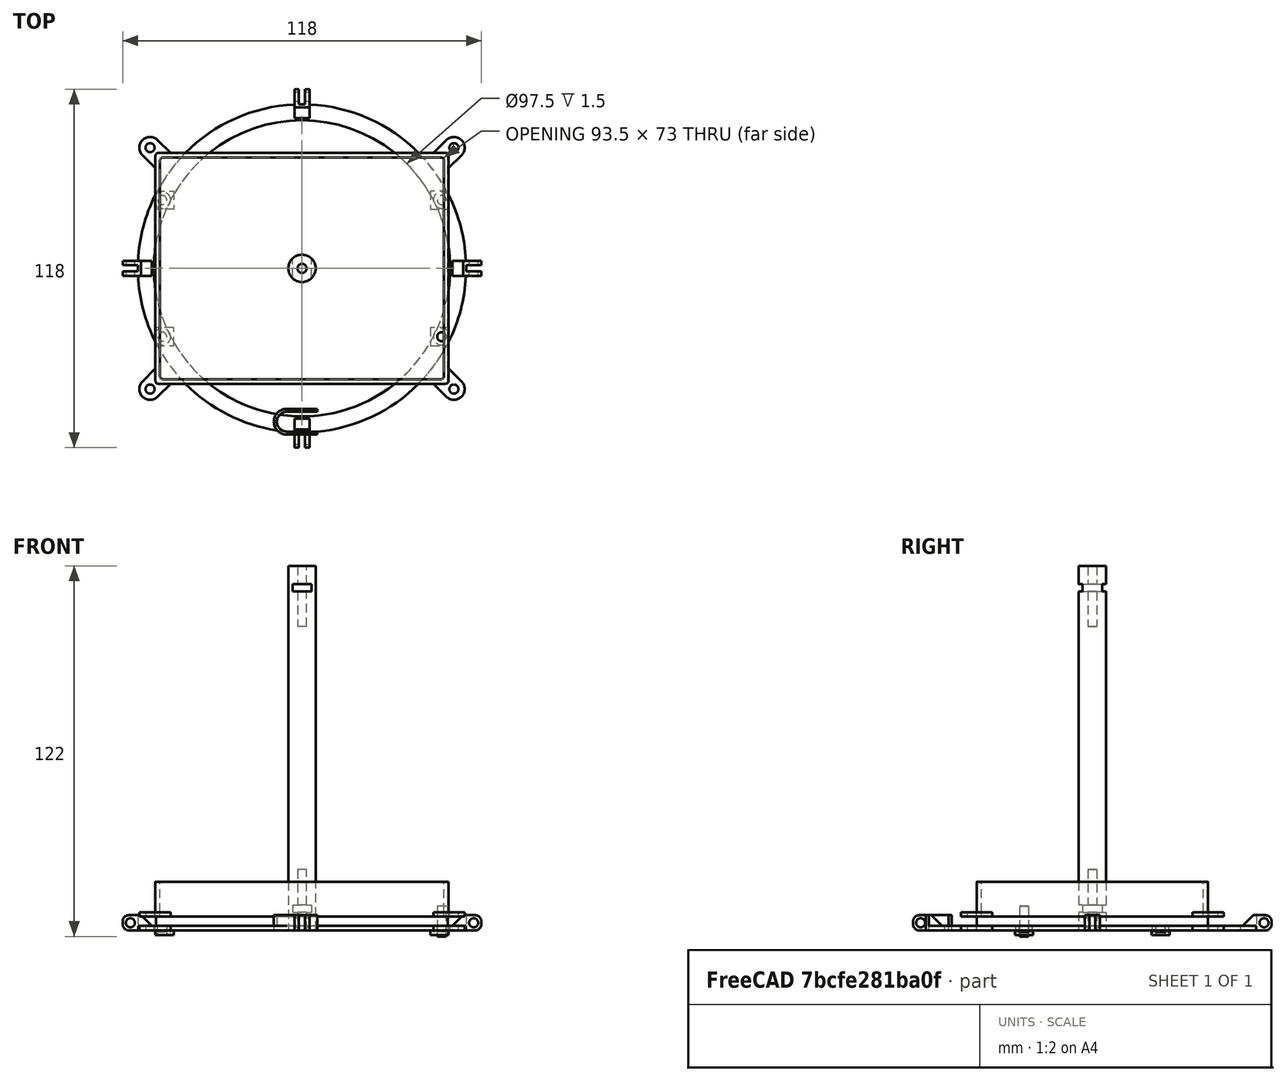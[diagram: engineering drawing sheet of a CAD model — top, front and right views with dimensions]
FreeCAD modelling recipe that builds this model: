
FCSTD DOCUMENT  (FreeCAD 0.20R29177 (Git))
Label: LSC-holder04-Robot
License: All rights reserved
LicenseURL: http://en.wikipedia.org/wiki/All_rights_reserved
objects: Part::Cut×12, Part::Box×11, Sketcher::SketchObject×9, Part::Cylinder×8, PartDesign::Pad×6, PartDesign::Body×4, Part::Fillet×4, Part::Chamfer×4, Part::Fuse×4, PartDesign::Pocket×3, Mesh::Feature×2, Spreadsheet::Sheet×1, PartDesign::Fillet×1
note: 76 computed .brp shape members not serialized (recipe doc carries the construction recipe); baked Part::Feature solids carry a one-line shape summary decoded from their .brp

FEATURE [Mesh::Feature] surface  label="ReferenceBase"
  Placement = pos=(50,-25.5,5.75) rot=(1,0,0;1.5708rad)
  expr: .Placement.Base.x = 0
FEATURE [Sketcher::SketchObject] Sketch  label="HolderBaseMain001"
  FullyConstrained = true
  MapMode = 5
  Support = -> [XY_Plane]
  expr: Constraints[2] = <<params>>.lcLength
  expr: Constraints[3] = <<params>>.lcWidth
  expr: Constraints[8] = <<params>>.lcWidth - 10
  expr: Constraints[9] = <<params>>.lcLength - 10
  sketch-geometry (24):
    g0: GeomPoint X=-48.25 Y=-38 Z=0
    g1: LineSegment StartX=-48.25 StartY=-33 StartZ=0 EndX=-48.25 EndY=33 EndZ=0
    g2: GeomPoint X=-48.25 Y=38 Z=0
    g3: LineSegment StartX=-43.25 StartY=38 StartZ=0 EndX=43.25 EndY=38 EndZ=0
    g4: GeomPoint X=48.25 Y=38 Z=0
    g5: LineSegment StartX=43.25 StartY=-38 StartZ=0 EndX=-43.25 EndY=-38 EndZ=0
    g6: LineSegment StartX=48.25 StartY=33 StartZ=0 EndX=48.25 EndY=-33 EndZ=0
    g7: GeomPoint X=48.25 Y=-38 Z=0
    g8: LineSegment StartX=43.25 StartY=-38 StartZ=0 EndX=47.4926 EndY=-42.2426 EndZ=0
    g9: LineSegment StartX=48.25 StartY=-33 StartZ=0 EndX=52.4926 EndY=-37.2426 EndZ=0
    g10: ArcOfCircle CenterX=49.9926 CenterY=-39.7426 CenterZ=0 NormalX=0 NormalY=0 NormalZ=1 AngleXU=0 Radius=3.53553 StartAngle=3.92699 EndAngle=7.06858
    g11: Circle CenterX=49.9926 CenterY=-39.7426 CenterZ=0 NormalX=0 NormalY=0 NormalZ=1 AngleXU=0 Radius=1.5
    g12: LineSegment StartX=43.25 StartY=38 StartZ=0 EndX=47.4926 EndY=42.2426 EndZ=0
    g13: LineSegment StartX=48.25 StartY=33 StartZ=0 EndX=52.4926 EndY=37.2426 EndZ=0
    g14: LineSegment StartX=-48.25 StartY=33 StartZ=0 EndX=-52.4926 EndY=37.2426 EndZ=0
    g15: LineSegment StartX=-43.25 StartY=38 StartZ=0 EndX=-47.4926 EndY=42.2426 EndZ=0
    g16: LineSegment StartX=-48.25 StartY=-33 StartZ=0 EndX=-52.4926 EndY=-37.2426 EndZ=0
    g17: LineSegment StartX=-43.25 StartY=-38 StartZ=0 EndX=-47.4926 EndY=-42.2426 EndZ=0
    g18: ArcOfCircle CenterX=49.9926 CenterY=39.7426 CenterZ=0 NormalX=0 NormalY=0 NormalZ=1 AngleXU=0 Radius=3.53553 StartAngle=5.49779 EndAngle=8.63938
    g19: ArcOfCircle CenterX=-49.9926 CenterY=39.7426 CenterZ=0 NormalX=0 NormalY=0 NormalZ=1 AngleXU=0 Radius=3.53553 StartAngle=0.785398 EndAngle=3.92699
    g20: ArcOfCircle CenterX=-49.9926 CenterY=-39.7426 CenterZ=0 NormalX=0 NormalY=0 NormalZ=1 AngleXU=0 Radius=3.53553 StartAngle=2.35619 EndAngle=5.49779
    g21: Circle CenterX=-49.9926 CenterY=-39.7426 CenterZ=0 NormalX=0 NormalY=0 NormalZ=1 AngleXU=0 Radius=1.5
    g22: Circle CenterX=-49.9926 CenterY=39.7426 CenterZ=0 NormalX=0 NormalY=0 NormalZ=1 AngleXU=0 Radius=1.5
    g23: Circle CenterX=49.9926 CenterY=39.7426 CenterZ=0 NormalX=0 NormalY=0 NormalZ=1 AngleXU=0 Radius=1.5
  constraints (64):
    c: Vertical(g1)
    c: Horizontal(g3)
    c: DistanceX(g2,g4) = 96.5
    c: DistanceY(g0,g2) = 76
    c: Horizontal(g5)
    c: Vertical(g6)
    c: Equal(g5,g3)
    c: Equal(g1,g6)
    c: DistanceY(g6,g6) = 66
    c: DistanceX(g3,g3) = 86.5
    c: DistanceX(g0) = -48.25
    c: DistanceY(g0) = -38
    c: DistanceX(g5) = -43.25
    c: DistanceY(g5) = -38
    c: DistanceX(g1) = -48.25
    c: DistanceY(g1) = -33
    c: Symmetric(g2,g7,g-1)
    c: Symmetric(g4,g0,g-1)
    c: Symmetric(g3,g5,g-1)
    c: Symmetric(g1,g6,g-1)
    c: Coincident(g8,g5)
    c: Coincident(g9,g6)
    c: Angle(g8) = -0.785398
    c: Angle(g9) = -0.785398
    c: Coincident(g10,g9)
    c: Coincident(g10,g8)
    c: Coincident(g11,g10)
    c: Distance(g8) = 6
    c: Diameter(g11) = 3
    c: Angle(g10) = 3.14159
    c: Coincident(g12,g3)
    c: Coincident(g13,g6)
    c: Coincident(g14,g1)
    c: Coincident(g15,g3)
    c: Angle(g13) = 0.785398
    c: Angle(g12) = 0.785398
    c: Angle(g15) = 2.35619
    c: Angle(g14) = 2.35619
    c: Coincident(g16,g1)
    c: Coincident(g17,g5)
    c: Angle(g16) = -2.35619
    c: Angle(g17) = -2.35619
    c: Equal(g16,g17)
    c: Equal(g17,g8)
    c: Equal(g8,g9)
    c: Equal(g9,g13)
    c: Equal(g13,g12)
    c: Equal(g12,g14)
    c: Equal(g14,g15)
    c: Coincident(g18,g12)
    c: Coincident(g18,g13)
    c: Angle(g18) = 3.14159
    c: Coincident(g19,g15)
    c: Coincident(g19,g14)
    c: Angle(g19) = 3.14159
    c: Coincident(g20,g16)
    c: Coincident(g20,g17)
    c: Angle(g20) = 3.14159
    c: Coincident(g21,g20)
    c: Diameter(g21) = 3
    c: Coincident(g22,g19)
    c: Diameter(g22) = 3
    c: Coincident(g23,g18)
    c: Diameter(g23) = 3
FEATURE [Spreadsheet::Sheet] Spreadsheet  label="params"
  cells = A2(lcLength)=96.5; A3(lcWidth)=76; A4(lcHeight)=2; A5(screwsHDist)=92; A6(screwsVDist)=45; A7(columnHeight)=120
FEATURE [PartDesign::Pad] Pad  label="HolderBaseMain"
  Direction = (0,0,1)
  Length = 1.5
  Length2 = 10
  Profile = -> Sketch
  ReferenceAxis = -> Sketch [N_Axis]
  Type = 0
FEATURE [Sketcher::SketchObject] Sketch001  label="ScrewsExtra001"
  FullyConstrained = true
  MapMode = 5
  Placement = pos=(0,0,0) rot=(1,0,0;3.14159rad)
  Support = -> [Pad]
  expr: Constraints[14] = (<<params>>.lcLength - <<params>>.screwsHDist) / 2
  expr: Constraints[25] = (<<params>>.lcLength - <<params>>.screwsHDist) / 2
  expr: Constraints[2] = <<params>>.screwsVDist
  expr: Constraints[3] = <<params>>.screwsHDist
  expr: Constraints[42] = (<<params>>.lcLength - <<params>>.screwsHDist) / 2
  expr: Constraints[43] = (<<params>>.lcLength - <<params>>.screwsHDist) / 2
  sketch-geometry (20):
    g0: GeomPoint X=-46 Y=22.5 Z=0
    g1: GeomPoint X=-46 Y=-22.5 Z=0
    g2: GeomPoint X=46 Y=-22.5 Z=0
    g3: GeomPoint X=46 Y=22.5 Z=0
    g4: LineSegment StartX=-48.25 StartY=25.5 StartZ=0 EndX=-42.25 EndY=25.5 EndZ=0
    g5: LineSegment StartX=-42.25 StartY=25.5 StartZ=0 EndX=-42.25 EndY=19.5 EndZ=0
    g6: LineSegment StartX=-42.25 StartY=19.5 StartZ=0 EndX=-48.25 EndY=19.5 EndZ=0
    g7: LineSegment StartX=-48.25 StartY=19.5 StartZ=0 EndX=-48.25 EndY=25.5 EndZ=0
    g8: LineSegment StartX=-42.25 StartY=-19.5 StartZ=0 EndX=-48.25 EndY=-19.5 EndZ=0
    g9: LineSegment StartX=-48.25 StartY=-19.5 StartZ=0 EndX=-48.25 EndY=-25.5 EndZ=0
    g10: LineSegment StartX=-48.25 StartY=-25.5 StartZ=0 EndX=-42.25 EndY=-25.5 EndZ=0
    g11: LineSegment StartX=-42.25 StartY=-25.5 StartZ=0 EndX=-42.25 EndY=-19.5 EndZ=0
    g12: LineSegment StartX=42.25 StartY=25.5 StartZ=0 EndX=48.25 EndY=25.5 EndZ=0
    g13: LineSegment StartX=48.25 StartY=25.5 StartZ=0 EndX=48.25 EndY=19.5 EndZ=0
    g14: LineSegment StartX=48.25 StartY=19.5 StartZ=0 EndX=42.25 EndY=19.5 EndZ=0
    g15: LineSegment StartX=42.25 StartY=19.5 StartZ=0 EndX=42.25 EndY=25.5 EndZ=0
    g16: LineSegment StartX=42.25 StartY=-19.5 StartZ=0 EndX=48.25 EndY=-19.5 EndZ=0
    g17: LineSegment StartX=48.25 StartY=-19.5 StartZ=0 EndX=48.25 EndY=-25.5 EndZ=0
    g18: LineSegment StartX=48.25 StartY=-25.5 StartZ=0 EndX=42.25 EndY=-25.5 EndZ=0
    g19: LineSegment StartX=42.25 StartY=-25.5 StartZ=0 EndX=42.25 EndY=-19.5 EndZ=0
  constraints (54):
    c: Symmetric(g0,g2,g-1)
    c: Symmetric(g3,g1,g-1)
    c: DistanceY(g2,g3) = 45
    c: DistanceX(g0,g3) = 92
    c: DistanceX(g2,g3) = 0
    c: DistanceY(g1,g2) = 0
    c: Coincident(g4,g5)
    c: Coincident(g5,g6)
    c: Coincident(g6,g7)
    c: Coincident(g7,g4)
    c: Horizontal(g4)
    c: Horizontal(g6)
    c: Vertical(g5)
    c: Vertical(g7)
    c: DistanceX(g4,g0) = 2.25
    c: DistanceY(g5,g5) = 6
    c: DistanceY(g0,g4) = 3
    c: Coincident(g8,g9)
    c: Coincident(g9,g10)
    c: Coincident(g10,g11)
    c: Coincident(g11,g8)
    c: Horizontal(g8)
    c: Horizontal(g10)
    c: Vertical(g9)
    c: Vertical(g11)
    c: DistanceX(g8,g1) = 2.25
    c: Coincident(g12,g13)
    c: Coincident(g13,g14)
    c: Coincident(g14,g15)
    c: Coincident(g15,g12)
    c: Horizontal(g12)
    c: Horizontal(g14)
    c: Vertical(g13)
    c: Vertical(g15)
    c: Coincident(g16,g17)
    c: Coincident(g17,g18)
    c: Coincident(g18,g19)
    c: Coincident(g19,g16)
    c: Horizontal(g16)
    c: Horizontal(g18)
    c: Vertical(g17)
    c: Vertical(g19)
    c: DistanceX(g3,g12) = 2.25
    c: DistanceX(g2,g16) = 2.25
    c: Equal(g4,g5)
    c: Equal(g5,g8)
    c: Equal(g8,g11)
    c: Equal(g11,g19)
    c: Equal(g19,g16)
    c: Equal(g16,g15)
    c: Equal(g15,g12)
    c: DistanceY(g1,g8) = 3
    c: DistanceY(g2,g16) = 3
    c: DistanceY(g3,g12) = 3
FEATURE [PartDesign::Pad] Pad001  label="ScrewsExtra"
  BaseFeature = -> Pad
  Direction = (0,0,-1)
  Length = 1.5
  Length2 = 10
  Profile = -> Sketch001
  ReferenceAxis = -> Sketch001 [N_Axis]
  Type = 0
FEATURE [Part::Cylinder] Cylinder  label="RefScrew"
  Angle = 360
  AttacherType = Attacher::AttachEngine3D
  FirstAngle = 0
  Height = 10
  Placement = pos=(46,-22.5,-2) rot=(0,0,1;0rad)
  Radius = 1.5
  SecondAngle = 0
FEATURE [Sketcher::SketchObject] Sketch002  label="ScrewsFull001"
  FullyConstrained = true
  MapMode = 5
  Placement = pos=(0,0,1.5) rot=(0,0,1;0rad)
  Support = -> [Pad001]
  expr: Constraints[2] = <<params>>.screwsHDist
  expr: Constraints[3] = <<params>>.screwsVDist
  sketch-geometry (4):
    g0: Circle CenterX=-46 CenterY=22.5 CenterZ=0 NormalX=0 NormalY=0 NormalZ=1 AngleXU=0 Radius=1.5
    g1: Circle CenterX=-46 CenterY=-22.5 CenterZ=0 NormalX=0 NormalY=0 NormalZ=1 AngleXU=0 Radius=1.5
    g2: Circle CenterX=46 CenterY=22.5 CenterZ=0 NormalX=0 NormalY=0 NormalZ=1 AngleXU=0 Radius=1.5
    g3: Circle CenterX=46 CenterY=-22.5 CenterZ=0 NormalX=0 NormalY=0 NormalZ=1 AngleXU=0 Radius=1.5
  constraints (10):
    c: Symmetric(g0,g3,g-1)
    c: Symmetric(g2,g1,g-1)
    c: DistanceX(g0,g2) = 92
    c: DistanceY(g3,g2) = 45
    c: DistanceX(g3,g2) = 0
    c: DistanceY(g1,g3) = 0
    c: Equal(g0,g1)
    c: Equal(g0,g3)
    c: Equal(g0,g2)
    c: Diameter(g0) = 3
FEATURE [PartDesign::Pocket] Pocket  label="ScrewsFull"
  BaseFeature = -> Pad001
  Direction = (0,0,-1)
  Length = 5
  Length2 = 5
  Profile = -> Sketch002
  ReferenceAxis = -> Sketch002 [N_Axis]
  Type = 1
FEATURE [Sketcher::SketchObject] Sketch003  label="ScrewsHead001"
  FullyConstrained = true
  MapMode = 5
  Placement = pos=(0,0,1.5) rot=(0,0,1;0rad)
  Support = -> [Pocket]
  expr: Constraints[2] = <<params>>.screwsVDist
  expr: Constraints[3] = <<params>>.screwsHDist
  sketch-geometry (4):
    g0: Circle CenterX=46 CenterY=22.5 CenterZ=0 NormalX=0 NormalY=0 NormalZ=1 AngleXU=0 Radius=2.75
    g1: Circle CenterX=-46 CenterY=22.5 CenterZ=0 NormalX=0 NormalY=0 NormalZ=1 AngleXU=0 Radius=2.75
    g2: Circle CenterX=-46 CenterY=-22.5 CenterZ=0 NormalX=0 NormalY=0 NormalZ=1 AngleXU=0 Radius=2.75
    g3: Circle CenterX=46 CenterY=-22.5 CenterZ=0 NormalX=0 NormalY=0 NormalZ=1 AngleXU=0 Radius=2.75
  constraints (10):
    c: Symmetric(g1,g3,g-1)
    c: Symmetric(g0,g2,g-1)
    c: DistanceY(g3,g0) = 45
    c: DistanceX(g1,g0) = 92
    c: DistanceX(g0,g3) = 0
    c: DistanceY(g3,g2) = 0
    c: Equal(g1,g0)
    c: Equal(g1,g2)
    c: Equal(g1,g3)
    c: Diameter(g1) = 5.5
FEATURE [PartDesign::Pocket] Pocket001  label="ScrewsHead"
  BaseFeature = -> Pocket
  Direction = (0,0,-1)
  Length = 2
  Length2 = 5
  Profile = -> Sketch003
  ReferenceAxis = -> Sketch003 [N_Axis]
  Type = 0
FEATURE [PartDesign::Body] Body  label="HolderBase"
  Group = -> [Sketch,Pad,Sketch001,Pad001,Sketch002,Pocket,Sketch003,Pocket001]
  Origin = -> Origin
  Tip = -> Pocket001
FEATURE [Sketcher::SketchObject] Sketch004  label="HolderMain001"
  FullyConstrained = true
  MapMode = 5
  Support = -> [XY_Plane001]
  sketch-geometry (8):
    g0: LineSegment StartX=-5 StartY=4.25 StartZ=0 EndX=5 EndY=4.25 EndZ=0
    g1: LineSegment StartX=5 StartY=4.25 StartZ=0 EndX=5 EndY=3.25 EndZ=0
    g2: LineSegment StartX=5 StartY=3.25 StartZ=0 EndX=-4.99602 EndY=3.25 EndZ=0
    g3: LineSegment StartX=4.99602 StartY=-3.25 StartZ=0 EndX=-5.00398 EndY=-3.25 EndZ=0
    g4: LineSegment StartX=-5.00002 StartY=-4.25 StartZ=0 EndX=4.99602 EndY=-4.25 EndZ=0
    g5: LineSegment StartX=4.99602 StartY=-4.25 StartZ=0 EndX=4.99602 EndY=-3.25 EndZ=0
    g6: ArcOfCircle CenterX=-5 CenterY=0 CenterZ=0 NormalX=0 NormalY=0 NormalZ=1 AngleXU=0 Radius=3.25 StartAngle=1.56957 EndAngle=4.71117
    g7: ArcOfCircle CenterX=-5 CenterY=0 CenterZ=0 NormalX=0 NormalY=0 NormalZ=1 AngleXU=0 Radius=4.25 StartAngle=1.5708 EndAngle=4.71238
  constraints (24):
    c: Coincident(g0,g1)
    c: Coincident(g1,g2)
    c: Horizontal(g0)
    c: Horizontal(g2)
    c: Vertical(g1)
    c: Coincident(g4,g5)
    c: Coincident(g5,g3)
    c: Horizontal(g3)
    c: Horizontal(g4)
    c: Vertical(g5)
    c: Symmetric(g2,g3,g-1)
    c: DistanceY(g3,g2) = 6.5
    c: Equal(g1,g5)
    c: DistanceY(g1,g1) = 1
    c: Equal(g0,g3)
    c: DistanceX(g0,g0) = 10
    c: DistanceX(g-1,g1) = 5
    c: PointOnObject(g6,g-1)
    c: Coincident(g6,g2)
    c: Coincident(g6,g3)
    c: Coincident(g7,g6)
    c: Coincident(g7,g0)
    c: Coincident(g7,g4)
    c: Angle(g6) = 3.14159
FEATURE [PartDesign::Pad] Pad002  label="HolderMain"
  Direction = (0,0,1)
  Length = 5
  Length2 = 10
  Profile = -> Sketch004
  ReferenceAxis = -> Sketch004 [N_Axis]
  Type = 0
FEATURE [PartDesign::Body] Body001  label="Holder"
  Group = -> [Sketch004,Pad002]
  Origin = -> Origin001
  Placement = pos=(0,-50.5,0) rot=(0,0,1;0rad)
  Tip = -> Pad002
FEATURE [Sketcher::SketchObject] Sketch005  label="CSHolderBase001"
  FullyConstrained = true
  MapMode = 5
  Support = -> [XY_Plane002]
  sketch-geometry (2):
    g0: Circle CenterX=0 CenterY=0 CenterZ=0 NormalX=0 NormalY=0 NormalZ=1 AngleXU=0 Radius=54
    g1: Circle CenterX=0 CenterY=0 CenterZ=0 NormalX=0 NormalY=0 NormalZ=1 AngleXU=0 Radius=48.75
  constraints (4):
    c: Coincident(g1,g-1)
    c: Coincident(g0,g1)
    c: Diameter(g1) = 97.5
    c: Diameter(g0) = 108
FEATURE [PartDesign::Pad] Pad003  label="CSHolderBase"
  Direction = (0,0,1)
  Length = 1.5
  Length2 = 10
  Profile = -> Sketch005
  ReferenceAxis = -> Sketch005 [N_Axis]
  Type = 0
FEATURE [Sketcher::SketchObject] Sketch006  label="CSHolderBase002"
  FullyConstrained = true
  MapMode = 5
  Placement = pos=(0,0,1.5) rot=(0,0,1;0rad)
  Support = -> [Pad003]
  sketch-geometry (4):
    g0: Circle CenterX=46 CenterY=22.5 CenterZ=0 NormalX=0 NormalY=0 NormalZ=1 AngleXU=0 Radius=1.5
    g1: Circle CenterX=-46 CenterY=-22.5 CenterZ=0 NormalX=0 NormalY=0 NormalZ=1 AngleXU=0 Radius=1.5
    g2: Circle CenterX=-46 CenterY=22.5 CenterZ=0 NormalX=0 NormalY=0 NormalZ=1 AngleXU=0 Radius=1.5
    g3: Circle CenterX=46 CenterY=-22.5 CenterZ=0 NormalX=0 NormalY=0 NormalZ=1 AngleXU=0 Radius=1.5
  constraints (10):
    c: Symmetric(g0,g1,g-1)
    c: Symmetric(g2,g3,g-1)
    c: DistanceX(g2,g0) = 92
    c: DistanceX(g3,g0) = 0
    c: DistanceY(g1,g2) = 45
    c: DistanceY(g3,g1) = 0
    c: Equal(g0,g2)
    c: Equal(g0,g1)
    c: Equal(g0,g3)
    c: Diameter(g0) = 3
FEATURE [PartDesign::Pocket] Pocket002  label="CSHolderHoles"
  BaseFeature = -> Pad003
  Direction = (0,0,-1)
  Length = 5
  Length2 = 5
  Profile = -> Sketch006
  ReferenceAxis = -> Sketch006 [N_Axis]
  Type = 1
FEATURE [PartDesign::Body] Body002  label="CSHolder"
  Group = -> [Sketch005,Pad003,Sketch006,Pocket002]
  Origin = -> Origin002
  Tip = -> Pocket002
FEATURE [Part::Box] Box  label="ExtLeg"
  AttacherType = Attacher::AttachEngine3D
  Height = 10
  Length = 5
  Width = 5
FEATURE [Part::Box] Box001  label="ExtLegHole"
  AttacherType = Attacher::AttachEngine3D
  Height = 5
  Length = 5
  Placement = pos=(0,1.5,5) rot=(0,0,1;0rad)
  Width = 2
FEATURE [Part::Cut] Cut  label="ExtLegTmp"
  Base = -> Box
  Tool = -> Box001
FEATURE [Part::Cylinder] Cylinder001  label="Screw"
  Angle = 360
  AttacherType = Attacher::AttachEngine3D
  FirstAngle = 0
  Height = 10
  Placement = pos=(2.5,-2.75,7.5) rot=(0.57735,0.57735,0.57735;4.18879rad)
  Radius = 1.5
  SecondAngle = 0
FEATURE [Part::Cut] Cut001
  Base = -> Cut
  Tool = -> Cylinder001
FEATURE [Part::Fillet] Fillet  label="ScrewExtTmp"
  Base = -> Cut001
  Edges = 4 edges r=2: [Edge1,Edge5,Edge10,Edge21]
  Placement = pos=(49,-2.5,5) rot=(0,1,0;1.5708rad)
FEATURE [Part::Chamfer] Chamfer  label="ScrewExt"
  Base = -> Fillet
  Edges = 1 edges r=4: [Edge4]
FEATURE [Part::Box] Box004  label="ExtLeg002"
  AttacherType = Attacher::AttachEngine3D
  Height = 10
  Length = 5
  Width = 5
FEATURE [Part::Box] Box005  label="ExtLegHole002"
  AttacherType = Attacher::AttachEngine3D
  Height = 5
  Length = 5
  Placement = pos=(0,1.5,5) rot=(0,0,1;0rad)
  Width = 2
FEATURE [Part::Cut] Cut004  label="ExtLegTmp002"
  Base = -> Box004
  Tool = -> Box005
FEATURE [Part::Cylinder] Cylinder003  label="Screw002"
  Angle = 360
  AttacherType = Attacher::AttachEngine3D
  FirstAngle = 0
  Height = 10
  Placement = pos=(2.5,-2.75,7.5) rot=(0.57735,0.57735,0.57735;4.18879rad)
  Radius = 1.5
  SecondAngle = 0
FEATURE [Part::Cut] Cut005
  Base = -> Cut004
  Tool = -> Cylinder003
FEATURE [Part::Fillet] Fillet002  label="ScrewExtTmp002"
  Base = -> Cut005
  Edges = 4 edges r=2: [Edge1,Edge5,Edge10,Edge21]
  Placement = pos=(49,-2.5,5) rot=(0,1,0;1.5708rad)
FEATURE [Part::Chamfer] Chamfer002  label="ScrewExt002"
  Base = -> Fillet002
  Edges = 1 edges r=4: [Edge4]
  Placement = pos=(0,0,0) rot=(0,0,1;1.5708rad)
FEATURE [Part::Box] Box006  label="ExtLeg003"
  AttacherType = Attacher::AttachEngine3D
  Height = 10
  Length = 5
  Width = 5
FEATURE [Part::Box] Box007  label="ExtLegHole003"
  AttacherType = Attacher::AttachEngine3D
  Height = 5
  Length = 5
  Placement = pos=(0,1.5,5) rot=(0,0,1;0rad)
  Width = 2
FEATURE [Part::Cut] Cut006  label="ExtLegTmp003"
  Base = -> Box006
  Tool = -> Box007
FEATURE [Part::Cylinder] Cylinder004  label="Screw003"
  Angle = 360
  AttacherType = Attacher::AttachEngine3D
  FirstAngle = 0
  Height = 10
  Placement = pos=(2.5,-2.75,7.5) rot=(0.57735,0.57735,0.57735;4.18879rad)
  Radius = 1.5
  SecondAngle = 0
FEATURE [Part::Cut] Cut007
  Base = -> Cut006
  Tool = -> Cylinder004
FEATURE [Part::Fillet] Fillet003  label="ScrewExtTmp003"
  Base = -> Cut007
  Edges = 4 edges r=2: [Edge1,Edge5,Edge10,Edge21]
  Placement = pos=(49,-2.5,5) rot=(0,1,0;1.5708rad)
FEATURE [Part::Chamfer] Chamfer003  label="ScrewExt003"
  Base = -> Fillet003
  Edges = 1 edges r=4: [Edge4]
  Placement = pos=(0,0,0) rot=(0,0,1;3.14159rad)
FEATURE [Part::Box] Box008  label="ExtLeg004"
  AttacherType = Attacher::AttachEngine3D
  Height = 10
  Length = 5
  Width = 5
FEATURE [Part::Box] Box009  label="ExtLegHole004"
  AttacherType = Attacher::AttachEngine3D
  Height = 5
  Length = 5
  Placement = pos=(0,1.5,5) rot=(0,0,1;0rad)
  Width = 2
FEATURE [Part::Cut] Cut008  label="ExtLegTmp004"
  Base = -> Box008
  Tool = -> Box009
FEATURE [Part::Cylinder] Cylinder005  label="Screw004"
  Angle = 360
  AttacherType = Attacher::AttachEngine3D
  FirstAngle = 0
  Height = 10
  Placement = pos=(2.5,-2.75,7.5) rot=(0.57735,0.57735,0.57735;4.18879rad)
  Radius = 1.5
  SecondAngle = 0
FEATURE [Part::Cut] Cut009
  Base = -> Cut008
  Tool = -> Cylinder005
FEATURE [Part::Fillet] Fillet004  label="ScrewExtTmp004"
  Base = -> Cut009
  Edges = 4 edges r=2: [Edge1,Edge5,Edge10,Edge21]
  Placement = pos=(49,-2.5,5) rot=(0,1,0;1.5708rad)
FEATURE [Part::Chamfer] Chamfer004  label="ScrewExt004"
  Base = -> Fillet004
  Edges = 1 edges r=4: [Edge4]
  Placement = pos=(0,0,0) rot=(0,0,-1;1.5708rad)
FEATURE [Part::Fuse] Fusion
  Base = -> Body002
  Tool = -> Chamfer
FEATURE [Part::Fuse] Fusion001
  Base = -> Chamfer002
  Tool = -> Fusion
FEATURE [Part::Fuse] Fusion002
  Base = -> Chamfer003
  Tool = -> Fusion001
FEATURE [Part::Fuse] Fusion003  label="FinalCSHolder"
  Base = -> Chamfer004
  Tool = -> Fusion002
FEATURE [Mesh::Feature] columnas  label="ReferenceColumn"
  Placement = pos=(0,0,0) rot=(1,0,0;1.5708rad)
FEATURE [Part::Cylinder] Cylinder006  label="ColumnMain"
  Angle = 360
  AttacherType = Attacher::AttachEngine3D
  FirstAngle = 0
  Height = 120
  Radius = 4.5
  SecondAngle = 0
  expr: Height = <<params>>.columnHeight
FEATURE [Part::Cylinder] Cylinder007  label="ColumnHole1"
  Angle = 360
  AttacherType = Attacher::AttachEngine3D
  FirstAngle = 0
  Height = 20
  Radius = 1.5
  SecondAngle = 0
FEATURE [Part::Box] Box010  label="Nut1"
  AttacherType = Attacher::AttachEngine3D
  Height = 2.4
  Length = 6.2
  Placement = pos=(-3.1,-5,6) rot=(0,0,1;0rad)
  Width = 10
FEATURE [Part::Box] Box011  label="Nut2"
  AttacherType = Attacher::AttachEngine3D
  Height = 2.4
  Length = 6.2
  Placement = pos=(-3.1,-5,111.6) rot=(0,0,1;0rad)
  Width = 10
  expr: .Placement.Base.z = <<params>>.columnHeight - 6 - 2.4
FEATURE [Part::Box] Box012  label="LSC"
  AttacherType = Attacher::AttachEngine3D
  Height = 3
  Length = 96
  Placement = pos=(-48,-38,1.5) rot=(0,0,1;0rad)
  Width = 76
  expr: Length = 96
  expr: Width = 76
FEATURE [Part::Cylinder] Cylinder008  label="ColumnHole2"
  Angle = 360
  AttacherType = Attacher::AttachEngine3D
  FirstAngle = 0
  Height = 20
  Placement = pos=(0,0,100) rot=(0,0,1;0rad)
  Radius = 1.5
  SecondAngle = 0
  expr: .Placement.Base.z = <<params>>.columnHeight - 20
FEATURE [Part::Cut] Cut010  label="ColumnTmp1"
  Base = -> Cylinder006
  Tool = -> Cylinder007
FEATURE [Part::Cut] Cut011  label="ColumnTmp2"
  Base = -> Cut010
  Tool = -> Cylinder008
FEATURE [Part::Cut] Cut012  label="ColumnTmp3"
  Base = -> Cut011
  Tool = -> Box011
FEATURE [Part::Cut] Cut013  label="Column"
  Base = -> Cut012
  Tool = -> Box010
FEATURE [Sketcher::SketchObject] Sketch007  label="HolderTopMain001"
  FullyConstrained = true
  MapMode = 5
  Support = -> [XY_Plane003]
  expr: Constraints[2] = <<params>>.lcLength
  expr: Constraints[3] = <<params>>.lcWidth
  expr: Constraints[73] = <<params>>.lcLength - 3
  expr: Constraints[74] = <<params>>.lcWidth - 3
  expr: Constraints[8] = <<params>>.lcWidth - 10
  expr: Constraints[9] = <<params>>.lcLength - 10
  sketch-geometry (28):
    g0: GeomPoint X=-48.25 Y=-38 Z=0
    g1: LineSegment StartX=-48.25 StartY=-33 StartZ=0 EndX=-48.25 EndY=33 EndZ=0
    g2: GeomPoint X=-48.25 Y=38 Z=0
    g3: LineSegment StartX=-43.25 StartY=38 StartZ=0 EndX=43.25 EndY=38 EndZ=0
    g4: GeomPoint X=48.25 Y=38 Z=0
    g5: LineSegment StartX=43.25 StartY=-38 StartZ=0 EndX=-43.25 EndY=-38 EndZ=0
    g6: LineSegment StartX=48.25 StartY=33 StartZ=0 EndX=48.25 EndY=-33 EndZ=0
    g7: GeomPoint X=48.25 Y=-38 Z=0
    g8: LineSegment StartX=43.25 StartY=-38 StartZ=0 EndX=47.4926 EndY=-42.2426 EndZ=0
    g9: LineSegment StartX=48.25 StartY=-33 StartZ=0 EndX=52.4926 EndY=-37.2426 EndZ=0
    g10: ArcOfCircle CenterX=49.9926 CenterY=-39.7426 CenterZ=0 NormalX=0 NormalY=0 NormalZ=1 AngleXU=0 Radius=3.53553 StartAngle=3.92699 EndAngle=7.06858
    g11: Circle CenterX=49.9926 CenterY=-39.7426 CenterZ=0 NormalX=0 NormalY=0 NormalZ=1 AngleXU=0 Radius=1.5
    g12: LineSegment StartX=43.25 StartY=38 StartZ=0 EndX=47.4926 EndY=42.2426 EndZ=0
    g13: LineSegment StartX=48.25 StartY=33 StartZ=0 EndX=52.4926 EndY=37.2426 EndZ=0
    g14: LineSegment StartX=-48.25 StartY=33 StartZ=0 EndX=-52.4926 EndY=37.2426 EndZ=0
    g15: LineSegment StartX=-43.25 StartY=38 StartZ=0 EndX=-47.4926 EndY=42.2426 EndZ=0
    g16: LineSegment StartX=-48.25 StartY=-33 StartZ=0 EndX=-52.4926 EndY=-37.2426 EndZ=0
    g17: LineSegment StartX=-43.25 StartY=-38 StartZ=0 EndX=-47.4926 EndY=-42.2426 EndZ=0
    g18: ArcOfCircle CenterX=49.9926 CenterY=39.7426 CenterZ=0 NormalX=0 NormalY=0 NormalZ=1 AngleXU=0 Radius=3.53553 StartAngle=5.49779 EndAngle=8.63938
    g19: ArcOfCircle CenterX=-49.9926 CenterY=39.7426 CenterZ=0 NormalX=0 NormalY=0 NormalZ=1 AngleXU=0 Radius=3.53553 StartAngle=0.785398 EndAngle=3.92699
    g20: ArcOfCircle CenterX=-49.9926 CenterY=-39.7426 CenterZ=0 NormalX=0 NormalY=0 NormalZ=1 AngleXU=0 Radius=3.53553 StartAngle=2.35619 EndAngle=5.49779
    g21: Circle CenterX=-49.9926 CenterY=-39.7426 CenterZ=0 NormalX=0 NormalY=0 NormalZ=1 AngleXU=0 Radius=1.5
    g22: Circle CenterX=-49.9926 CenterY=39.7426 CenterZ=0 NormalX=0 NormalY=0 NormalZ=1 AngleXU=0 Radius=1.5
    g23: Circle CenterX=49.9926 CenterY=39.7426 CenterZ=0 NormalX=0 NormalY=0 NormalZ=1 AngleXU=0 Radius=1.5
    g24: LineSegment StartX=-46.75 StartY=36.5 StartZ=0 EndX=46.75 EndY=36.5 EndZ=0
    g25: LineSegment StartX=46.75 StartY=36.5 StartZ=0 EndX=46.75 EndY=-36.5 EndZ=0
    g26: LineSegment StartX=46.75 StartY=-36.5 StartZ=0 EndX=-46.75 EndY=-36.5 EndZ=0
    g27: LineSegment StartX=-46.75 StartY=-36.5 StartZ=0 EndX=-46.75 EndY=36.5 EndZ=0
  constraints (75):
    c: Vertical(g1)
    c: Horizontal(g3)
    c: DistanceX(g2,g4) = 96.5
    c: DistanceY(g0,g2) = 76
    c: Horizontal(g5)
    c: Vertical(g6)
    c: Equal(g5,g3)
    c: Equal(g1,g6)
    c: DistanceY(g6,g6) = 66
    c: DistanceX(g3,g3) = 86.5
    c: DistanceX(g0) = -48.25
    c: DistanceY(g0) = -38
    c: DistanceX(g5) = -43.25
    c: DistanceY(g5) = -38
    c: DistanceX(g1) = -48.25
    c: DistanceY(g1) = -33
    c: Symmetric(g2,g7,g-1)
    c: Symmetric(g4,g0,g-1)
    c: Symmetric(g3,g5,g-1)
    c: Symmetric(g1,g6,g-1)
    c: Coincident(g8,g5)
    c: Coincident(g9,g6)
    c: Angle(g8) = -0.785398
    c: Angle(g9) = -0.785398
    c: Coincident(g10,g9)
    c: Coincident(g10,g8)
    c: Coincident(g11,g10)
    c: Distance(g8) = 6
    c: Diameter(g11) = 3
    c: Angle(g10) = 3.14159
    c: Coincident(g12,g3)
    c: Coincident(g13,g6)
    c: Coincident(g14,g1)
    c: Coincident(g15,g3)
    c: Angle(g13) = 0.785398
    c: Angle(g12) = 0.785398
    c: Angle(g15) = 2.35619
    c: Angle(g14) = 2.35619
    c: Coincident(g16,g1)
    c: Coincident(g17,g5)
    c: Angle(g16) = -2.35619
    c: Angle(g17) = -2.35619
    c: Equal(g16,g17)
    c: Equal(g17,g8)
    c: Equal(g8,g9)
    c: Equal(g9,g13)
    c: Equal(g13,g12)
    c: Equal(g12,g14)
    c: Equal(g14,g15)
    c: Coincident(g18,g12)
    c: Coincident(g18,g13)
    c: Angle(g18) = 3.14159
    c: Coincident(g19,g15)
    c: Coincident(g19,g14)
    c: Angle(g19) = 3.14159
    c: Coincident(g20,g16)
    c: Coincident(g20,g17)
    c: Angle(g20) = 3.14159
    c: Coincident(g21,g20)
    c: Diameter(g21) = 3
    c: Coincident(g22,g19)
    c: Diameter(g22) = 3
    c: Coincident(g23,g18)
    c: Diameter(g23) = 3
    c: Coincident(g24,g25)
    c: Coincident(g25,g26)
    c: Coincident(g26,g27)
    c: Coincident(g27,g24)
    c: Horizontal(g24)
    c: Horizontal(g26)
    c: Vertical(g25)
    c: Vertical(g27)
    c: Symmetric(g24,g25,g-1)
    c: DistanceX(g24,g24) = 93.5
    c: DistanceY(g25,g25) = 73
FEATURE [PartDesign::Pad] Pad004  label="HolderTopMain"
  Direction = (0,0,1)
  Length = 1.5
  Length2 = 10
  Profile = -> Sketch007
  ReferenceAxis = -> Sketch007 [N_Axis]
  Type = 0
FEATURE [Sketcher::SketchObject] Sketch008  label="HolderBlock001"
  FullyConstrained = true
  MapMode = 5
  Placement = pos=(0,0,1.5) rot=(0,0,1;0rad)
  Support = -> [Pad004]
  expr: Constraints[10] = <<params>>.lcWidth
  expr: Constraints[20] = <<params>>.lcLength - 3
  expr: Constraints[21] = <<params>>.lcWidth - 3
  expr: Constraints[9] = <<params>>.lcLength
  sketch-geometry (8):
    g0: LineSegment StartX=48.25 StartY=38 StartZ=0 EndX=-48.25 EndY=38 EndZ=0
    g1: LineSegment StartX=-48.25 StartY=38 StartZ=0 EndX=-48.25 EndY=-38 EndZ=0
    g2: LineSegment StartX=-48.25 StartY=-38 StartZ=0 EndX=48.25 EndY=-38 EndZ=0
    g3: LineSegment StartX=48.25 StartY=-38 StartZ=0 EndX=48.25 EndY=38 EndZ=0
    g4: LineSegment StartX=-46.75 StartY=36.5 StartZ=0 EndX=46.75 EndY=36.5 EndZ=0
    g5: LineSegment StartX=46.75 StartY=36.5 StartZ=0 EndX=46.75 EndY=-36.5 EndZ=0
    g6: LineSegment StartX=46.75 StartY=-36.5 StartZ=0 EndX=-46.75 EndY=-36.5 EndZ=0
    g7: LineSegment StartX=-46.75 StartY=-36.5 StartZ=0 EndX=-46.75 EndY=36.5 EndZ=0
  constraints (22):
    c: Coincident(g0,g1)
    c: Coincident(g1,g2)
    c: Coincident(g2,g3)
    c: Coincident(g3,g0)
    c: Horizontal(g0)
    c: Horizontal(g2)
    c: Vertical(g1)
    c: Vertical(g3)
    c: Symmetric(g0,g2,g-1)
    c: DistanceX(g0,g0) = 96.5
    c: DistanceY(g3,g3) = 76
    c: Coincident(g4,g5)
    c: Coincident(g5,g6)
    c: Coincident(g6,g7)
    c: Coincident(g7,g4)
    c: Horizontal(g4)
    c: Horizontal(g6)
    c: Vertical(g5)
    c: Vertical(g7)
    c: Symmetric(g4,g6,g-1)
    c: DistanceX(g4,g4) = 93.5
    c: DistanceY(g5,g5) = 73
FEATURE [PartDesign::Pad] Pad005  label="HolderBlock"
  BaseFeature = -> Pad004
  Direction = (0,0,1)
  Length = 10
  Length2 = 10
  Profile = -> Sketch008
  ReferenceAxis = -> Sketch008 [N_Axis]
  Type = 0
FEATURE [PartDesign::Fillet] Fillet005  label="SoftTop"
  Base = -> Pad005 [Edge79,Edge39,Edge83,Edge38,Edge95,Edge93,Edge94,Edge96]
  BaseFeature = -> Pad005
  Radius = 1
  SupportTransform = false
  UseAllEdges = false
FEATURE [PartDesign::Body] Body003  label="HolderTop"
  Group = -> [Sketch007,Pad004,Sketch008,Pad005,Fillet005]
  Origin = -> Origin003
  Placement = pos=(0,0,4.5) rot=(0,0.707107,0.707107;0rad)
  Tip = -> Fillet005
